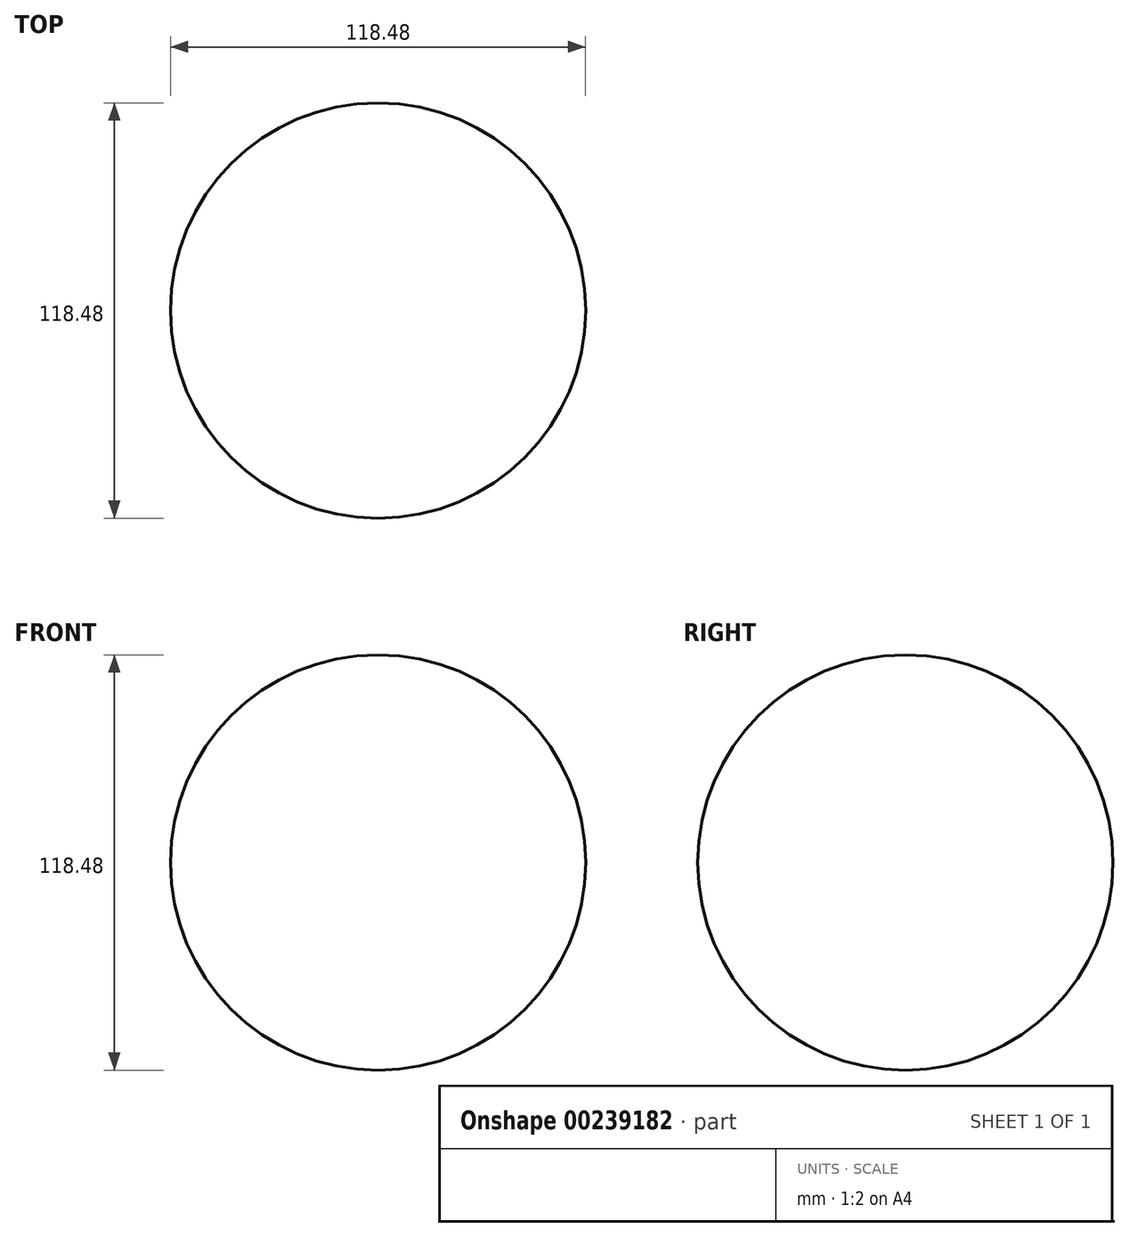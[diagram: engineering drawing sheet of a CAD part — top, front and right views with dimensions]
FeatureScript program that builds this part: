
annotation { "Feature Type Name" : "Feature", "Feature Type Description" : "" }
export const myFeature = defineFeature(function(context is Context, id is Id, definition is map)
    precondition{}
    {
        {
            var Q0;
            Q0=qCreatedBy(makeId("Front.planeOp"),FACE);
            var sketch = newSketch(context, id + "F0", { "sketchPlane" : qUnion([Q0])});
            skArc(sketch, "E0", {"start": v(0, -59.24) * mm, "mid": v(59.24, 0) * mm, "end": v(0, 59.24) * mm});
            skLineSegment(sketch, "E1", {"start": v(0, 59.24) * mm, "end": v(0, -59.24) * mm});
            skSolve(sketch);
        }
        {
            var Q0;
            Q0 = qSketchRegion(id + "F0", true);
            var Q1;
            Q1=sQuery(id+"F0.wireOp",EDGE,"E1");
            revolve(context, id + "F1", {"entities" : qUnion([Q0]), "axis" : qUnion([Q1]), "revolveType" : RevolveType.FULL});
        }
    });
